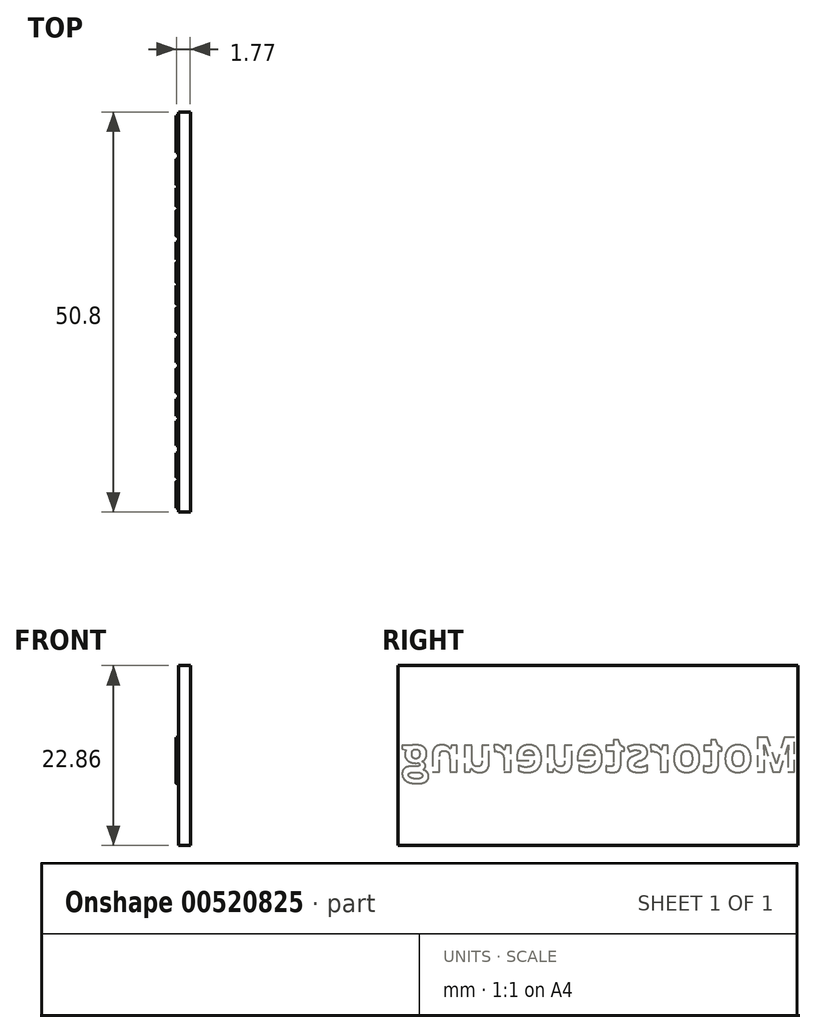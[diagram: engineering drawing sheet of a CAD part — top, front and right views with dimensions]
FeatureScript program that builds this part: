
annotation { "Feature Type Name" : "Feature", "Feature Type Description" : "" }
export const myFeature = defineFeature(function(context is Context, id is Id, definition is map)
    precondition{}
    {
        {
            var Q0;
            Q0=qCreatedBy(makeId("Right.planeOp"),FACE);
            var sketch = newSketch(context, id + "F0", { "sketchPlane" : qUnion([Q0])});
            skLineSegment(sketch, "E0.bottom", {"start": v(0, 0) * mm, "end": v(50.8, 0) * mm});
            skLineSegment(sketch, "E0.top", {"start": v(0, 22.86) * mm, "end": v(50.8, 22.86) * mm});
            skLineSegment(sketch, "E0.left", {"start": v(0, 0) * mm, "end": v(0, 22.86) * mm});
            skLineSegment(sketch, "E0.right", {"start": v(50.8, 0) * mm, "end": v(50.8, 22.86) * mm});
            skSolve(sketch);
        }
        {
            var Q0;
            Q0=makeQuery(id+"F0.imprint","IMPRINT",FACE,{"disambiguationData":[TD([[makeQuery(id+"F0.imprint","IMPRINT",EDGE,{"derivedFrom":sQuery(id+"F0.wireOp",EDGE,"E0.bottom")}),1.0]])]});
            extrude(context, id + "F1", {"entities" : qUnion([Q0]), "depth" : 1.52 * mm, "offsetDistance" : 25.4 * mm});
        }
        {
            var Q0;
            Q0=makeQuery(id+"F1.opExtrude","CAP_FACE",FACE,{"disambiguationData":[OSD([sQuery(id+"F0.wireOp",EDGE,"E0.bottom"),sQuery(id+"F0.wireOp",EDGE,"E0.top"),sQuery(id+"F0.wireOp",EDGE,"E0.left"),sQuery(id+"F0.wireOp",EDGE,"E0.right")])],"isStart":true});
            var sketch = newSketch(context, id + "F2", { "sketchPlane" : qUnion([Q0])});
            skText(sketch, "E1", { "text": "Motorsteuerung", "fontName": "OpenSans-Bold.ttf"});
            const initialGuessF2  = {"E1": [-0.05094, 0.00934, 1, 0, 0.00445]};
            skSetInitialGuess(sketch, initialGuessF2);
            skSolve(sketch);
        }
        {
            var Q0;
            Q0=makeQuery(id+"F2.imprint","IMPRINT",FACE,{"disambiguationData":[TD([[makeQuery(id+"F2.imprint","IMPRINT",EDGE,{"derivedFrom":sQuery(id+"F2.wireOp",EDGE,"E1.sketch_text.stroke-0")}),-1.0]])]});
            var Q1;
            Q1=makeQuery(id+"F2.imprint","IMPRINT",FACE,{"disambiguationData":[TD([[makeQuery(id+"F2.imprint","IMPRINT",EDGE,{"derivedFrom":sQuery(id+"F2.wireOp",EDGE,"E1.sketch_text.stroke-19")}),-1.0]])]});
            var Q2;
            Q2=makeQuery(id+"F2.imprint","IMPRINT",FACE,{"disambiguationData":[TD([[makeQuery(id+"F2.imprint","IMPRINT",EDGE,{"derivedFrom":sQuery(id+"F2.wireOp",EDGE,"E1.sketch_text.stroke-37")}),-1.0]])]});
            var Q3;
            Q3=makeQuery(id+"F2.imprint","IMPRINT",FACE,{"disambiguationData":[TD([[makeQuery(id+"F2.imprint","IMPRINT",EDGE,{"derivedFrom":sQuery(id+"F2.wireOp",EDGE,"E1.sketch_text.stroke-55")}),-1.0]])]});
            var Q4;
            Q4=makeQuery(id+"F2.imprint","IMPRINT",FACE,{"disambiguationData":[TD([[makeQuery(id+"F2.imprint","IMPRINT",EDGE,{"derivedFrom":sQuery(id+"F2.wireOp",EDGE,"E1.sketch_text.stroke-73")}),-1.0]])]});
            var Q5;
            Q5=makeQuery(id+"F2.imprint","IMPRINT",FACE,{"disambiguationData":[TD([[makeQuery(id+"F2.imprint","IMPRINT",EDGE,{"derivedFrom":sQuery(id+"F2.wireOp",EDGE,"E1.sketch_text.stroke-86")}),-1.0]])]});
            var Q6;
            Q6=makeQuery(id+"F2.imprint","IMPRINT",FACE,{"disambiguationData":[TD([[makeQuery(id+"F2.imprint","IMPRINT",EDGE,{"derivedFrom":sQuery(id+"F2.wireOp",EDGE,"E1.sketch_text.stroke-112")}),-1.0]])]});
            var Q7;
            Q7=makeQuery(id+"F2.imprint","IMPRINT",FACE,{"disambiguationData":[TD([[makeQuery(id+"F2.imprint","IMPRINT",EDGE,{"derivedFrom":sQuery(id+"F2.wireOp",EDGE,"E1.sketch_text.stroke-130")}),-1.0]])]});
            var Q8;
            Q8=makeQuery(id+"F2.imprint","IMPRINT",FACE,{"disambiguationData":[TD([[makeQuery(id+"F2.imprint","IMPRINT",EDGE,{"derivedFrom":sQuery(id+"F2.wireOp",EDGE,"E1.sketch_text.stroke-150")}),-1.0]])]});
            var Q9;
            Q9=makeQuery(id+"F2.imprint","IMPRINT",FACE,{"disambiguationData":[TD([[makeQuery(id+"F2.imprint","IMPRINT",EDGE,{"derivedFrom":sQuery(id+"F2.wireOp",EDGE,"E1.sketch_text.stroke-167")}),-1.0]])]});
            var Q10;
            Q10=makeQuery(id+"F2.imprint","IMPRINT",FACE,{"disambiguationData":[TD([[makeQuery(id+"F2.imprint","IMPRINT",EDGE,{"derivedFrom":sQuery(id+"F2.wireOp",EDGE,"E1.sketch_text.stroke-187")}),-1.0]])]});
            var Q11;
            Q11=makeQuery(id+"F2.imprint","IMPRINT",FACE,{"disambiguationData":[TD([[makeQuery(id+"F2.imprint","IMPRINT",EDGE,{"derivedFrom":sQuery(id+"F2.wireOp",EDGE,"E1.sketch_text.stroke-200")}),-1.0]])]});
            var Q12;
            Q12=makeQuery(id+"F2.imprint","IMPRINT",FACE,{"disambiguationData":[TD([[makeQuery(id+"F2.imprint","IMPRINT",EDGE,{"derivedFrom":sQuery(id+"F2.wireOp",EDGE,"E1.sketch_text.stroke-217")}),-1.0]])]});
            var Q13;
            Q13=makeQuery(id+"F2.imprint","IMPRINT",FACE,{"disambiguationData":[TD([[makeQuery(id+"F2.imprint","IMPRINT",EDGE,{"derivedFrom":sQuery(id+"F2.wireOp",EDGE,"E1.sketch_text.stroke-234")}),-1.0]])]});
            extrude(context, id + "F3", {"entities" : qUnion([Q0, Q1, Q2, Q3, Q4, Q5, Q6, Q7, Q8, Q9, Q10, Q11, Q12, Q13]), "operationType" : NewBodyOperationType.ADD, "depth" : 0.25 * mm, "offsetDistance" : 25.4 * mm});
        }
    });
